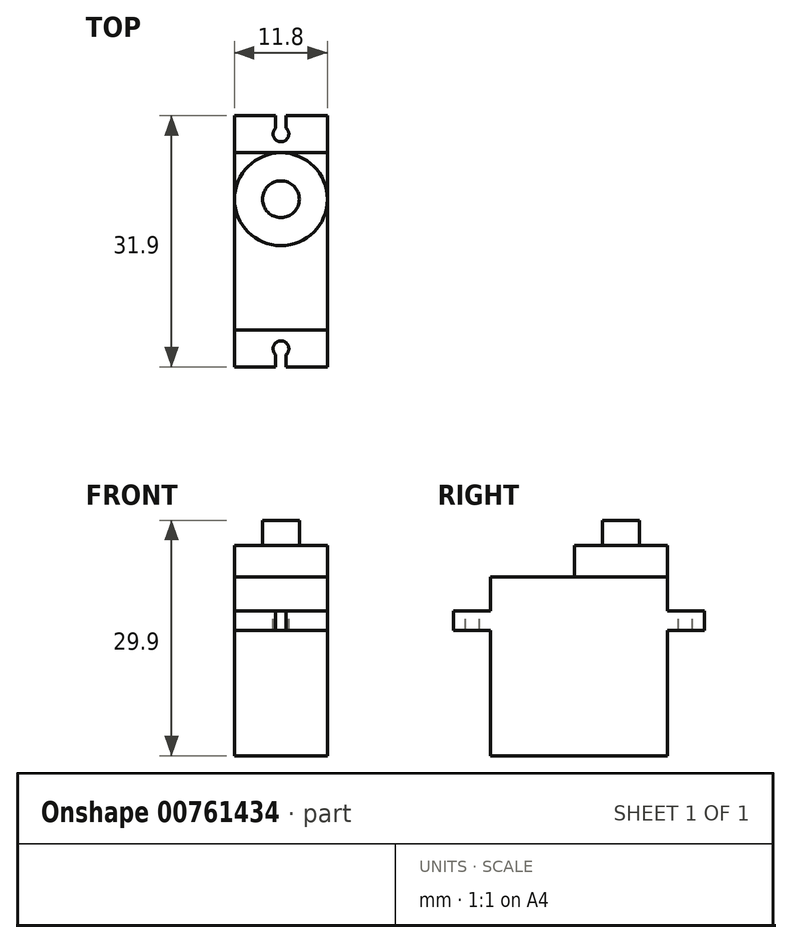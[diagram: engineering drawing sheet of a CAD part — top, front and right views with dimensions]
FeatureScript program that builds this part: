
annotation { "Feature Type Name" : "Feature", "Feature Type Description" : "" }
export const myFeature = defineFeature(function(context is Context, id is Id, definition is map)
    precondition{}
    {
        {
            var Q0;
            Q0=qCreatedBy(makeId("Top.planeOp"),FACE);
            var sketch = newSketch(context, id + "F0", { "sketchPlane" : qUnion([Q0])});
            skLineSegment(sketch, "E0.bottom", {"start": v(5.9, 11.25) * mm, "end": v(-5.9, 11.25) * mm});
            skLineSegment(sketch, "E0.top", {"start": v(5.9, -11.25) * mm, "end": v(-5.9, -11.25) * mm});
            skLineSegment(sketch, "E0.left", {"start": v(5.9, 11.25) * mm, "end": v(5.9, -11.25) * mm});
            skLineSegment(sketch, "E0.right", {"start": v(-5.9, 11.25) * mm, "end": v(-5.9, -11.25) * mm});
            skPoint(sketch, "E0.middle", {"position": v(0, 0) * mm});
            skSolve(sketch);
        }
        {
            var Q0;
            Q0=makeQuery(id+"F0.imprint","IMPRINT",FACE,{"disambiguationData":[TD([[makeQuery(id+"F0.imprint","IMPRINT",EDGE,{"derivedFrom":sQuery(id+"F0.wireOp",EDGE,"E0.bottom")}),1.0]])]});
            extrude(context, id + "F1", {"entities" : qUnion([Q0]), "depth" : 15.9 * mm, "offsetDistance" : 25.4 * mm});
        }
        {
            var Q0;
            Q0=makeQuery(id+"F1.opExtrude","CAP_FACE",FACE,{"disambiguationData":[OSD([sQuery(id+"F0.wireOp",EDGE,"E0.bottom"),sQuery(id+"F0.wireOp",EDGE,"E0.top"),sQuery(id+"F0.wireOp",EDGE,"E0.left"),sQuery(id+"F0.wireOp",EDGE,"E0.right")])],"isStart":false});
            var sketch = newSketch(context, id + "F2", { "sketchPlane" : qUnion([Q0])});
            skLineSegment(sketch, "E1.bottom", {"start": v(5.9, 15.95) * mm, "end": v(-5.9, 15.95) * mm});
            skLineSegment(sketch, "E1.top", {"start": v(5.9, -15.95) * mm, "end": v(-5.9, -15.95) * mm});
            skLineSegment(sketch, "E1.left", {"start": v(5.9, 15.95) * mm, "end": v(5.9, -15.95) * mm});
            skLineSegment(sketch, "E1.right", {"start": v(-5.9, 15.95) * mm, "end": v(-5.9, -15.95) * mm});
            skPoint(sketch, "E1.middle", {"position": v(0, 0) * mm});
            skSolve(sketch);
        }
        {
            var Q0;
            Q0 = qSketchRegion(id + "F2", true);
            extrude(context, id + "F3", {"entities" : qUnion([Q0]), "operationType" : NewBodyOperationType.ADD, "depth" : 2.5 * mm, "offsetDistance" : 25.4 * mm});
        }
        {
            var Q0;
            Q0=makeQuery(id+"F3.opExtrude","CAP_FACE",FACE,{"disambiguationData":[OSD([sQuery(id+"F2.wireOp",EDGE,"E1.bottom"),sQuery(id+"F2.wireOp",EDGE,"E1.top"),sQuery(id+"F2.wireOp",EDGE,"E1.left"),sQuery(id+"F2.wireOp",EDGE,"E1.right")])],"isStart":false});
            var sketch = newSketch(context, id + "F4", { "sketchPlane" : qUnion([Q0])});
            skCircle(sketch, "E2", {"center": v(0, 13.65) * mm, "radius": 1 * mm});
            skCircle(sketch, "E3", {"center": v(0, -13.65) * mm, "radius": 1 * mm});
            skLineSegment(sketch, "E4.bottom", {"start": v(-0.66, -15.95) * mm, "end": v(0.66, -15.95) * mm});
            skLineSegment(sketch, "E4.top", {"start": v(-0.66, -13.65) * mm, "end": v(0.66, -13.65) * mm});
            skLineSegment(sketch, "E4.left", {"start": v(-0.66, -15.95) * mm, "end": v(-0.66, -13.65) * mm});
            skLineSegment(sketch, "E4.right", {"start": v(0.67, -15.95) * mm, "end": v(0.67, -13.65) * mm});
            skLineSegment(sketch, "E5.bottom", {"start": v(-0.67, 15.95) * mm, "end": v(0.67, 15.95) * mm});
            skLineSegment(sketch, "E5.top", {"start": v(-0.67, 13.65) * mm, "end": v(0.67, 13.65) * mm});
            skLineSegment(sketch, "E5.left", {"start": v(-0.67, 15.95) * mm, "end": v(-0.67, 13.65) * mm});
            skLineSegment(sketch, "E5.right", {"start": v(0.66, 15.95) * mm, "end": v(0.66, 13.65) * mm});
            skSolve(sketch);
        }
        {
            var Q0;
            Q0 = qSketchRegion(id + "F4", true);
            extrude(context, id + "F5", {"entities" : qUnion([Q0]), "operationType" : NewBodyOperationType.REMOVE, "oppositeDirection" : true, "depth" : 2.5 * mm, "offsetDistance" : 25.4 * mm});
        }
        {
            var Q0;
            Q0 = qSketchRegion(id + "F0", true);
            extrude(context, id + "F6", {"entities" : qUnion([Q0]), "operationType" : NewBodyOperationType.ADD, "depth" : 22.7 * mm, "offsetDistance" : 25.4 * mm});
        }
        {
            var Q0;
            Q0=makeQuery(id+"F6.opExtrude","CAP_FACE",FACE,{"disambiguationData":[OSD([sQuery(id+"F0.wireOp",EDGE,"E0.bottom"),sQuery(id+"F0.wireOp",EDGE,"E0.top"),sQuery(id+"F0.wireOp",EDGE,"E0.left"),sQuery(id+"F0.wireOp",EDGE,"E0.right")])],"isStart":false});
            var sketch = newSketch(context, id + "F7", { "sketchPlane" : qUnion([Q0])});
            skCircle(sketch, "E6", {"center": v(0, 5.35) * mm, "radius": 5.9 * mm});
            skSolve(sketch);
        }
        {
            var Q0;
            {var subQ0=sQuery(id+"F7.wireOp",EDGE,"E6");var subQ1=makeQuery(id+"F7.imprint","INTERSECT",VERTEX,{"derivedFrom":[makeQuery(id+"F6.opExtrude","CAP_EDGE",EDGE,{"disambiguationData":[OSD([sQuery(id+"F0.wireOp",EDGE,"E0.bottom")])],"isStart":false}),subQ0]});Q0=makeQuery(id+"F7.imprint","IMPRINT",FACE,{"disambiguationData":[TD([[makeQuery(id+"F7.imprint","IMPRINT",EDGE,{"disambiguationData":[TD([[subQ1,1.0]])],"derivedFrom":subQ0}),1.0]])]});}
            extrude(context, id + "F8", {"entities" : qUnion([Q0]), "operationType" : NewBodyOperationType.ADD, "depth" : 4 * mm, "offsetDistance" : 25.4 * mm});
        }
        {
            var Q0;
            Q0=makeQuery(id+"F8.opExtrude","CAP_FACE",FACE,{"disambiguationData":[OSD([sQuery(id+"F7.wireOp",EDGE,"E6")])],"isStart":false});
            var sketch = newSketch(context, id + "F9", { "sketchPlane" : qUnion([Q0])});
            skCircle(sketch, "E7", {"center": v(0, 5.35) * mm, "radius": 2.33 * mm});
            skSolve(sketch);
        }
        {
            var Q0;
            Q0=makeQuery(id+"F9.imprint","IMPRINT",FACE,{"disambiguationData":[TD([[makeQuery(id+"F9.imprint","IMPRINT",EDGE,{"derivedFrom":sQuery(id+"F9.wireOp",EDGE,"E7")}),1.0]])]});
            extrude(context, id + "F10", {"entities" : qUnion([Q0]), "operationType" : NewBodyOperationType.ADD, "depth" : 3.2 * mm, "offsetDistance" : 25.4 * mm});
        }
    });
